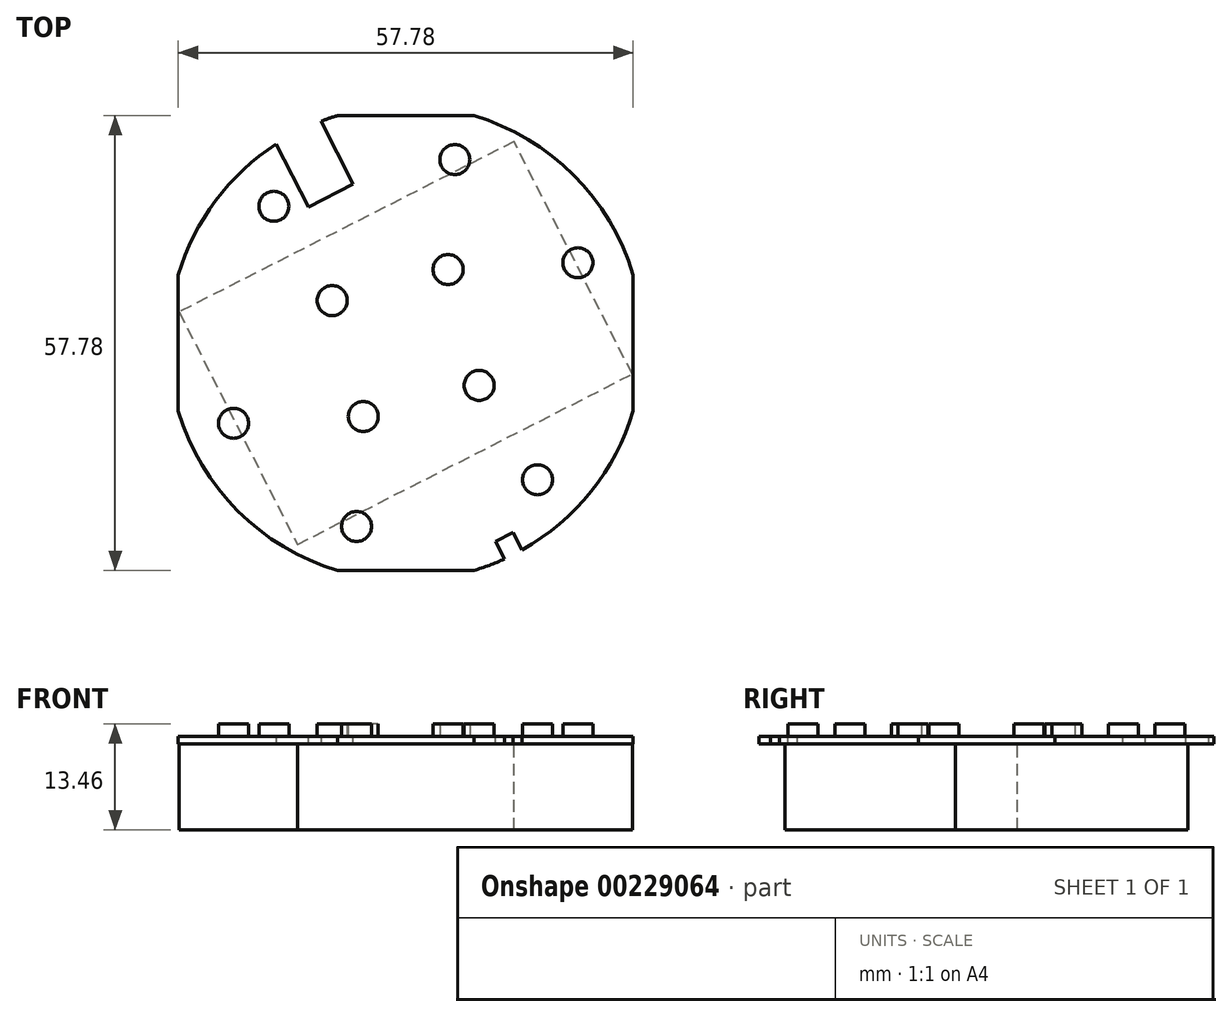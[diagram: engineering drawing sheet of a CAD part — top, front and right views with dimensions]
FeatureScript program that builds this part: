
annotation { "Feature Type Name" : "Feature", "Feature Type Description" : "" }
export const myFeature = defineFeature(function(context is Context, id is Id, definition is map)
    precondition{}
    {
        {
            var Q0;
            Q0=qCreatedBy(makeId("Top.planeOp"),FACE);
            var sketch = newSketch(context, id + "F0", { "sketchPlane" : qUnion([Q0])});
            skCircle(sketch, "E0", {"center": v(0, 0) * mm, "radius": 30.16 * mm});
            skSolve(sketch);
        }
        {
            var Q0;
            Q0=qSketchRegion(id+"F0",true);
            extrude(context, id + "F1", {"entities" : qUnion([Q0]), "depth" : 0.97 * mm});
        }
        {
            var Q0;
            Q0=qCreatedBy(makeId("Top.planeOp"),FACE);
            var sketch = newSketch(context, id + "F2", { "sketchPlane" : qUnion([Q0])});
            skLineSegment(sketch, "E1.bottom", {"start": v(28.9, -28.9) * mm, "end": v(-28.9, -28.9) * mm});
            skLineSegment(sketch, "E1.top", {"start": v(28.9, 28.9) * mm, "end": v(-28.9, 28.9) * mm});
            skLineSegment(sketch, "E1.left", {"start": v(28.9, -28.9) * mm, "end": v(28.9, 28.9) * mm});
            skLineSegment(sketch, "E1.right", {"start": v(-28.9, -28.9) * mm, "end": v(-28.9, 28.9) * mm});
            skPoint(sketch, "E1.middle", {"position": v(0, 0) * mm});
            skLineSegment(sketch, "E2.bottom", {"start": v(38.1, -38.1) * mm, "end": v(-38.1, -38.1) * mm});
            skLineSegment(sketch, "E2.top", {"start": v(38.1, 38.1) * mm, "end": v(-38.1, 38.1) * mm});
            skLineSegment(sketch, "E2.left", {"start": v(38.1, -38.1) * mm, "end": v(38.1, 38.1) * mm});
            skLineSegment(sketch, "E2.right", {"start": v(-38.1, -38.1) * mm, "end": v(-38.1, 38.1) * mm});
            skSolve(sketch);
        }
        {
            var Q0;
            Q0 = qSketchRegion(id + "F2", true);
            extrude(context, id + "F3", {"entities" : qUnion([Q0]), "operationType" : NewBodyOperationType.REMOVE, "endBound" : BoundingType.THROUGH_ALL, "depth" : 25.4 * mm});
        }
        {
            var Q0;
            Q0=makeQuery(id+"F1.opExtrude","CAP_FACE",FACE,{"disambiguationData":[OSD([sQuery(id+"F0.wireOp",EDGE,"E0")])],"isStart":false});
            var sketch = newSketch(context, id + "F4", { "sketchPlane" : qUnion([Q0])});
            skLineSegment(sketch, "E3.bottom", {"start": v(9.33, -5.39) * mm, "end": v(-5.39, -9.33) * mm, "construction": true});
            skLineSegment(sketch, "E3.top", {"start": v(5.39, 9.33) * mm, "end": v(-9.33, 5.39) * mm, "construction": true});
            skLineSegment(sketch, "E3.left", {"start": v(9.33, -5.39) * mm, "end": v(5.39, 9.33) * mm, "construction": true});
            skLineSegment(sketch, "E3.right", {"start": v(-5.39, -9.33) * mm, "end": v(-9.33, 5.39) * mm, "construction": true});
            skPoint(sketch, "E3.middle", {"position": v(0, 0) * mm});
            skCircle(sketch, "E4", {"center": v(-9.33, 5.39) * mm, "radius": 1.9 * mm});
            skCircle(sketch, "E5", {"center": v(5.39, 9.33) * mm, "radius": 1.9 * mm});
            skCircle(sketch, "E6", {"center": v(9.33, -5.39) * mm, "radius": 1.9 * mm});
            skCircle(sketch, "E7", {"center": v(-5.39, -9.33) * mm, "radius": 1.9 * mm});
            skLineSegment(sketch, "E8", {"start": v(-28.9, 0) * mm, "end": v(28.9, 0) * mm, "construction": true});
            skLineSegment(sketch, "E9", {"start": v(5.39, 9.33) * mm, "end": v(0, 0) * mm, "construction": true});
            skSolve(sketch);
        }
        {
            var Q0;
            Q0=qSketchRegion(id+"F4",true);
            extrude(context, id + "F5", {"entities" : qUnion([Q0]), "operationType" : NewBodyOperationType.ADD, "depth" : 1.57 * mm});
        }
        {
            var Q0;
            Q0=makeQuery(id+"F1.opExtrude","CAP_FACE",FACE,{"disambiguationData":[OSD([sQuery(id+"F0.wireOp",EDGE,"E0")])],"isStart":false});
            var sketch = newSketch(context, id + "F6", { "sketchPlane" : qUnion([Q0])});
            skLineSegment(sketch, "E10", {"start": v(-30.16, 0) * mm, "end": v(30.16, 0) * mm, "construction": true});
            skLineSegment(sketch, "E11", {"start": v(0, 30.16) * mm, "end": v(0, -30.16) * mm, "construction": true});
            skLineSegment(sketch, "E12.bottom", {"start": v(6.25, 23.3) * mm, "end": v(-16.75, 17.37) * mm, "construction": true});
            skLineSegment(sketch, "E12.top", {"start": v(16.75, -17.37) * mm, "end": v(-6.25, -23.3) * mm, "construction": true});
            skLineSegment(sketch, "E12.left", {"start": v(6.25, 23.3) * mm, "end": v(16.75, -17.37) * mm, "construction": true});
            skLineSegment(sketch, "E12.right", {"start": v(-16.75, 17.37) * mm, "end": v(-6.25, -23.3) * mm, "construction": true});
            skPoint(sketch, "E12.middle", {"position": v(0, 0) * mm});
            skLineSegment(sketch, "E13", {"start": v(6.25, 23.3) * mm, "end": v(-6.25, -23.3) * mm, "construction": true});
            skCircle(sketch, "E14", {"center": v(6.25, 23.3) * mm, "radius": 1.9 * mm});
            skCircle(sketch, "E15", {"center": v(-16.75, 17.37) * mm, "radius": 1.9 * mm});
            skCircle(sketch, "E16", {"center": v(-6.25, -23.3) * mm, "radius": 1.9 * mm});
            skCircle(sketch, "E17", {"center": v(16.75, -17.37) * mm, "radius": 1.9 * mm});
            skLineSegment(sketch, "E18", {"start": v(-21.87, -10.2) * mm, "end": v(21.87, 10.2) * mm, "construction": true});
            skCircle(sketch, "E19", {"center": v(21.87, 10.2) * mm, "radius": 1.9 * mm});
            skCircle(sketch, "E20", {"center": v(-21.87, -10.2) * mm, "radius": 1.9 * mm});
            skSolve(sketch);
        }
        {
            var Q0;
            Q0=qSketchRegion(id+"F6",true);
            extrude(context, id + "F7", {"entities" : qUnion([Q0]), "operationType" : NewBodyOperationType.ADD, "depth" : 1.57 * mm});
        }
        {
            var Q0;
            Q0=makeQuery(id+"F1.opExtrude","CAP_FACE",FACE,{"disambiguationData":[OSD([sQuery(id+"F0.wireOp",EDGE,"E0")])],"isStart":false});
            var sketch = newSketch(context, id + "F8", { "sketchPlane" : qUnion([Q0])});
            skLineSegment(sketch, "E21", {"start": v(-28.9, 0) * mm, "end": v(28.9, 0) * mm, "construction": true});
            skLineSegment(sketch, "E22", {"start": v(0, 0) * mm, "end": v(13.68, -26.88) * mm, "construction": true});
            skLineSegment(sketch, "E23", {"start": v(0, 0) * mm, "end": v(0, -28.9) * mm, "construction": true});
            skLineSegment(sketch, "E24", {"start": v(12.55, -27.46) * mm, "end": v(14.81, -26.3) * mm});
            skLineSegment(sketch, "E25", {"start": v(12.55, -27.46) * mm, "end": v(11.4, -25.2) * mm});
            skLineSegment(sketch, "E26", {"start": v(11.4, -25.2) * mm, "end": v(13.66, -24.04) * mm});
            skLineSegment(sketch, "E27", {"start": v(13.66, -24.04) * mm, "end": v(14.81, -26.3) * mm});
            skSolve(sketch);
        }
        {
            var Q0;
            Q0 = qSketchRegion(id + "F8", true);
            extrude(context, id + "F9", {"entities" : qUnion([Q0]), "operationType" : NewBodyOperationType.REMOVE, "oppositeDirection" : true, "depth" : 25.4 * mm});
        }
        {
            var Q0;
            Q0=makeQuery(id+"F1.opExtrude","CAP_FACE",FACE,{"disambiguationData":[OSD([sQuery(id+"F0.wireOp",EDGE,"E0")])],"isStart":false});
            var sketch = newSketch(context, id + "F10", { "sketchPlane" : qUnion([Q0])});
            skLineSegment(sketch, "E28", {"start": v(0, 28.9) * mm, "end": v(0, 0) * mm, "construction": true});
            skLineSegment(sketch, "E29", {"start": v(0, 0) * mm, "end": v(-13.68, 26.88) * mm, "construction": true});
            skLineSegment(sketch, "E30", {"start": v(-16.51, 25.44) * mm, "end": v(-10.85, 28.32) * mm});
            skLineSegment(sketch, "E31", {"start": v(-16.51, 25.44) * mm, "end": v(-12.36, 17.3) * mm});
            skLineSegment(sketch, "E32", {"start": v(-12.36, 17.3) * mm, "end": v(-6.7, 20.17) * mm});
            skLineSegment(sketch, "E33", {"start": v(-6.7, 20.17) * mm, "end": v(-10.85, 28.32) * mm});
            skSolve(sketch);
        }
        {
            var Q0;
            Q0 = qSketchRegion(id + "F10", true);
            extrude(context, id + "F11", {"entities" : qUnion([Q0]), "operationType" : NewBodyOperationType.REMOVE, "oppositeDirection" : true, "depth" : 25.4 * mm});
        }
        {
            var Q0;
            Q0=makeQuery(id+"F1.opExtrude","CAP_FACE",FACE,{"disambiguationData":[OSD([sQuery(id+"F0.wireOp",EDGE,"E0")])],"isStart":true});
            var sketch = newSketch(context, id + "F12", { "sketchPlane" : qUnion([Q0])});
            skLineSegment(sketch, "E34", {"start": v(13.75, -25.6) * mm, "end": v(-28.78, -3.95) * mm});
            skLineSegment(sketch, "E35", {"start": v(-28.78, -3.95) * mm, "end": v(-13.75, 25.6) * mm});
            skLineSegment(sketch, "E36", {"start": v(-13.75, 25.6) * mm, "end": v(28.78, 3.95) * mm});
            skLineSegment(sketch, "E37", {"start": v(28.78, 3.95) * mm, "end": v(13.75, -25.6) * mm});
            skLineSegment(sketch, "E38", {"start": v(-7.52, -14.77) * mm, "end": v(7.52, 14.77) * mm, "construction": true});
            skSolve(sketch);
        }
        {
            var Q0;
            Q0 = qSketchRegion(id + "F12", true);
            extrude(context, id + "F13", {"entities" : qUnion([Q0]), "operationType" : NewBodyOperationType.ADD, "depth" : 10.92 * mm});
        }
    });
